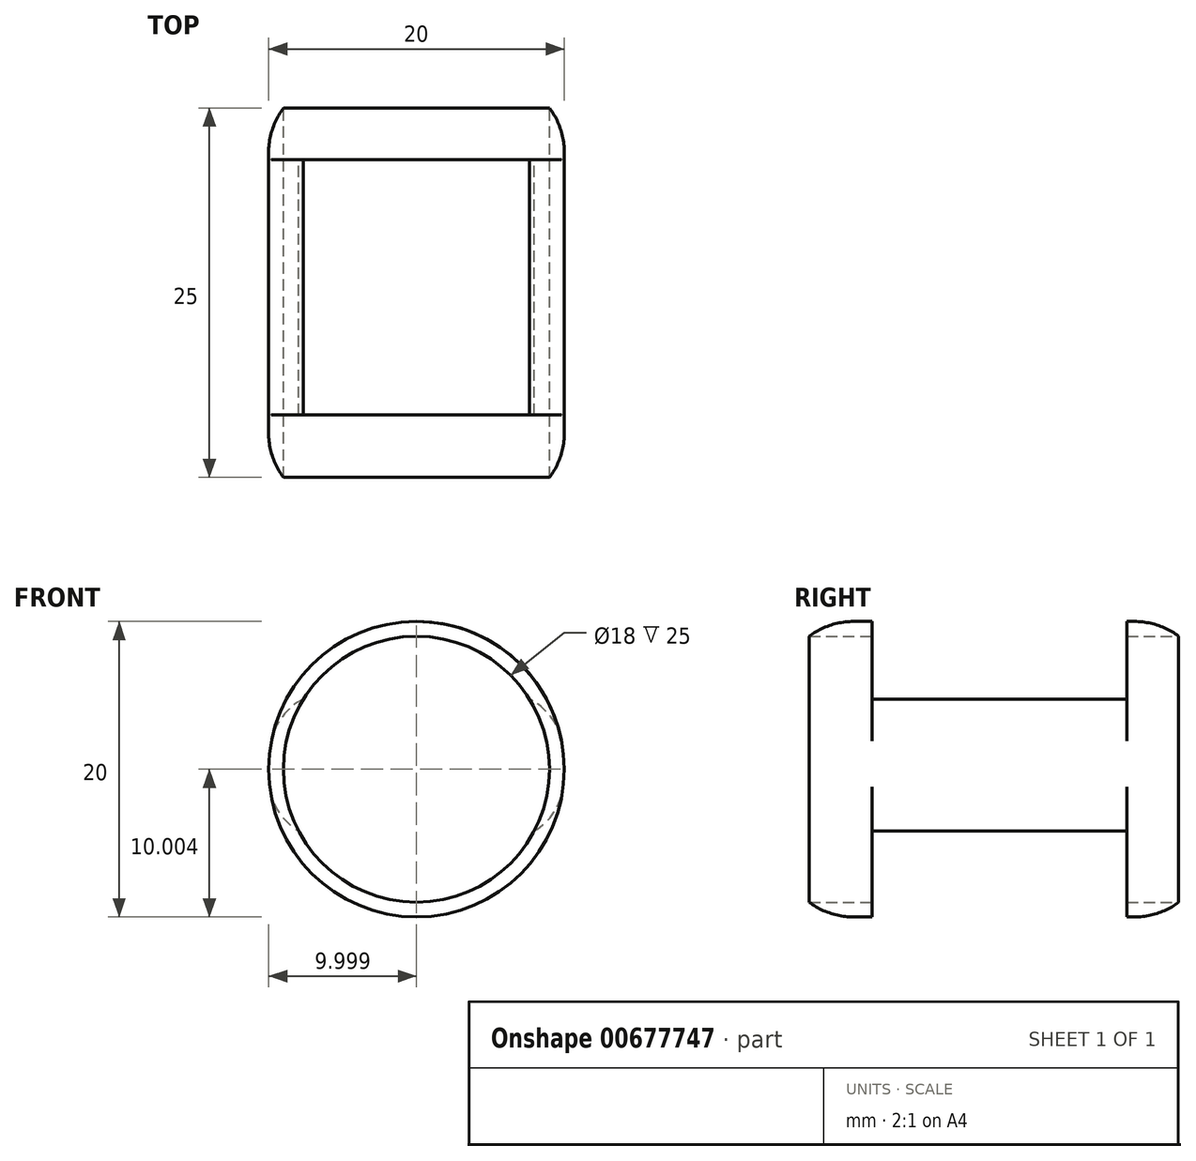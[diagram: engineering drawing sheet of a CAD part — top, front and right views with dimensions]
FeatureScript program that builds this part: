
annotation { "Feature Type Name" : "Feature", "Feature Type Description" : "" }
export const myFeature = defineFeature(function(context is Context, id is Id, definition is map)
    precondition{}
    {
        {
            var Q0;
            Q0=qCreatedBy(makeId("Front.planeOp"),FACE);
            var sketch = newSketch(context, id + "F0", { "sketchPlane" : qUnion([Q0])});
            skCircle(sketch, "E0", {"center": v(-49.94, 42.83) * mm, "radius": 10 * mm});
            skCircle(sketch, "E1", {"center": v(-49.94, 42.83) * mm, "radius": 9 * mm});
            skSolve(sketch);
        }
        {
            var Q0;
            Q0 = qSketchRegion(id + "F0", true);
            extrude(context, id + "F1", {"entities" : qUnion([Q0]), "depth" : 25 * mm, "offsetDistance" : 25 * mm});
        }
        {
            var Q0;
            Q0=qCreatedBy(makeId("Right.planeOp"),FACE);
            var sketch = newSketch(context, id + "F2", { "sketchPlane" : qUnion([Q0])});
            skLineSegment(sketch, "E2.bottom", {"start": v(-20.75, 54.02) * mm, "end": v(-3.5, 54.02) * mm});
            skLineSegment(sketch, "E2.top", {"start": v(-20.75, 47.57) * mm, "end": v(-3.5, 47.57) * mm});
            skLineSegment(sketch, "E2.left", {"start": v(-20.75, 54.02) * mm, "end": v(-20.75, 47.57) * mm});
            skLineSegment(sketch, "E2.right", {"start": v(-3.5, 54.02) * mm, "end": v(-3.5, 47.57) * mm});
            skLineSegment(sketch, "E3.bottom", {"start": v(-20.75, 29.95) * mm, "end": v(-3.5, 29.95) * mm});
            skLineSegment(sketch, "E3.top", {"start": v(-20.75, 38.66) * mm, "end": v(-3.5, 38.66) * mm});
            skLineSegment(sketch, "E3.left", {"start": v(-20.75, 29.95) * mm, "end": v(-20.75, 38.66) * mm});
            skLineSegment(sketch, "E3.right", {"start": v(-3.5, 29.95) * mm, "end": v(-3.5, 38.66) * mm});
            skSolve(sketch);
        }
        {
            var Q0;
            Q0 = qSketchRegion(id + "F2", true);
            extrude(context, id + "F3", {"entities" : qUnion([Q0]), "operationType" : NewBodyOperationType.REMOVE, "oppositeDirection" : true, "depth" : 200 * mm, "offsetDistance" : 25 * mm});
        }
        {
            var Q0;
            Q0=makeQuery(id+"F1.opExtrude","CAP_EDGE",EDGE,{"disambiguationData":[OSD([sQuery(id+"F0.wireOp",EDGE,"E0")])],"isStart":false});
            var Q1;
            Q1=makeQuery(id+"F1.opExtrude","CAP_EDGE",EDGE,{"disambiguationData":[OSD([sQuery(id+"F0.wireOp",EDGE,"E0")])],"isStart":true});
            fillet(context, id + "F4", {"entities" : qUnion([Q0, Q1]), "radius" : 5 * mm, "tangentPropagation" : true, "allowEdgeOverflow" : false});
        }
        {
            var Q0;
            Q0=makeQuery(id+"F3.boolean.opBoolean","INTERSECT",EDGE,{"disambiguationData":[OD(1.0)],"derivedFrom":[makeQuery(id+"F1.opExtrude","SWEPT_FACE",FACE,{"disambiguationData":[OSD([sQuery(id+"F0.wireOp",EDGE,"E0")])]}),makeQuery(id+"F3.opExtrude","SWEPT_FACE",FACE,{"disambiguationData":[OSD([sQuery(id+"F2.wireOp",EDGE,"E2.top")])]})]});
            var Q1;
            Q1=makeQuery(id+"F3.boolean.opBoolean","INTERSECT",EDGE,{"disambiguationData":[OD(0.0)],"derivedFrom":[makeQuery(id+"F1.opExtrude","SWEPT_FACE",FACE,{"disambiguationData":[OSD([sQuery(id+"F0.wireOp",EDGE,"E0")])]}),makeQuery(id+"F3.opExtrude","SWEPT_FACE",FACE,{"disambiguationData":[OSD([sQuery(id+"F2.wireOp",EDGE,"E2.top")])]})]});
            var Q2;
            Q2=makeQuery(id+"F3.boolean.opBoolean","INTERSECT",EDGE,{"disambiguationData":[OD(0.0)],"derivedFrom":[makeQuery(id+"F1.opExtrude","SWEPT_FACE",FACE,{"disambiguationData":[OSD([sQuery(id+"F0.wireOp",EDGE,"E0")])]}),makeQuery(id+"F3.opExtrude","SWEPT_FACE",FACE,{"disambiguationData":[OSD([sQuery(id+"F2.wireOp",EDGE,"E3.top")])]})]});
            var Q3;
            Q3=makeQuery(id+"F3.boolean.opBoolean","INTERSECT",EDGE,{"disambiguationData":[OD(1.0)],"derivedFrom":[makeQuery(id+"F1.opExtrude","SWEPT_FACE",FACE,{"disambiguationData":[OSD([sQuery(id+"F0.wireOp",EDGE,"E0")])]}),makeQuery(id+"F3.opExtrude","SWEPT_FACE",FACE,{"disambiguationData":[OSD([sQuery(id+"F2.wireOp",EDGE,"E3.top")])]})]});
            fillet(context, id + "F5", {"entities" : qUnion([Q0, Q1, Q2, Q3]), "radius" : 4 * mm, "tangentPropagation" : true, "allowEdgeOverflow" : false});
        }
    });
